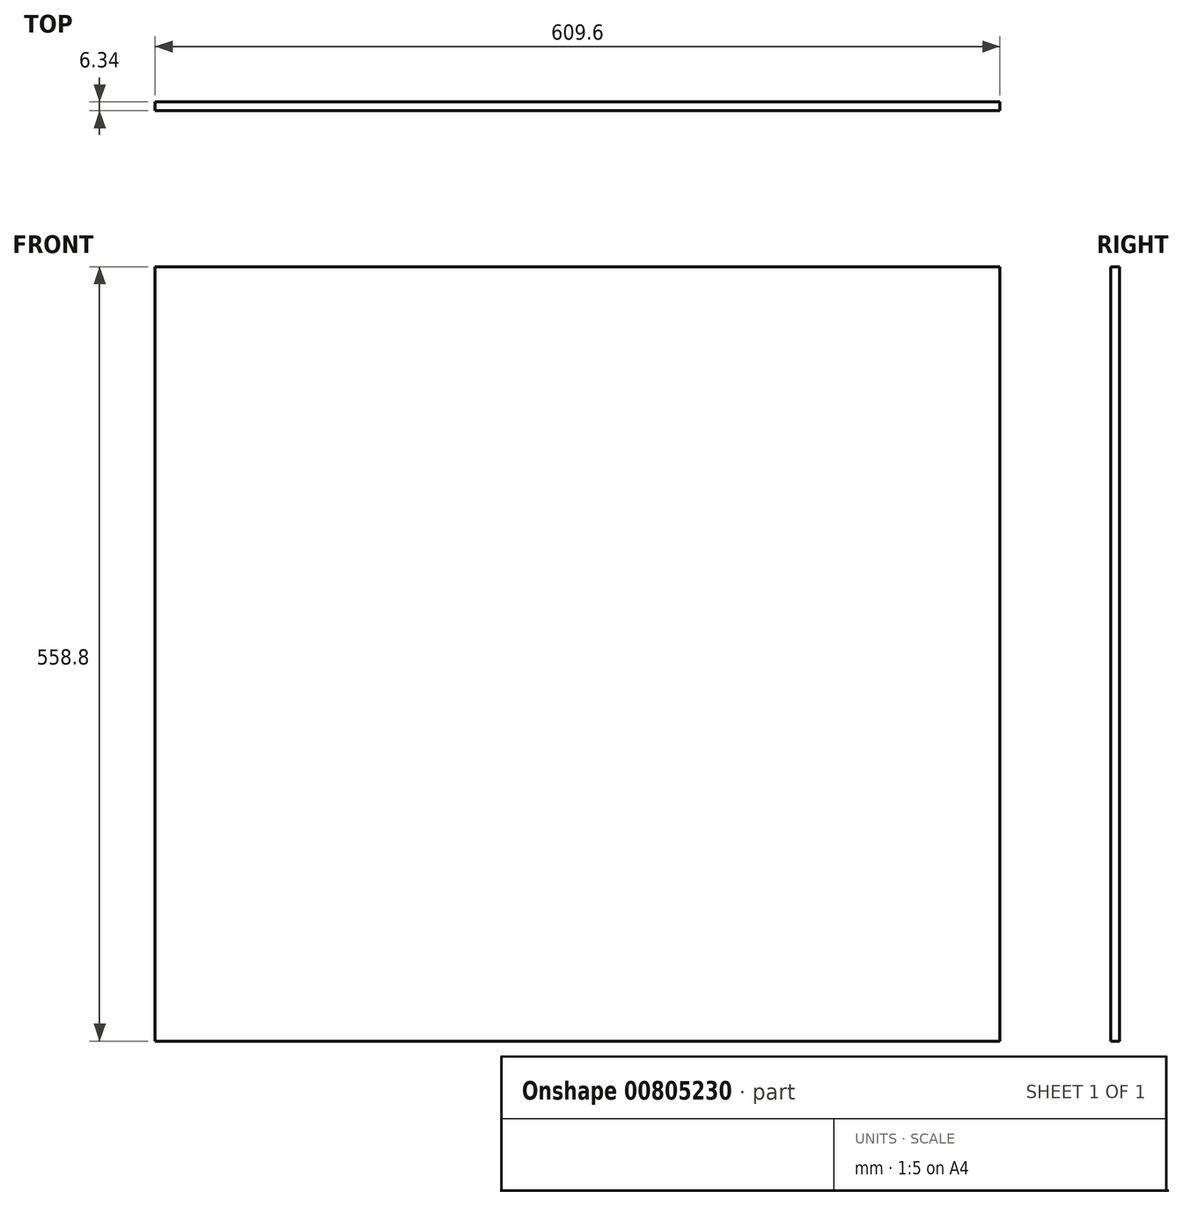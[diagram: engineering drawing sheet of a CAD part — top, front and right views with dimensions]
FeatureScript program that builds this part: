
annotation { "Feature Type Name" : "Feature", "Feature Type Description" : "" }
export const myFeature = defineFeature(function(context is Context, id is Id, definition is map)
    precondition{}
    {
        {
            var Q0;
            Q0=qCreatedBy(makeId("Front.planeOp"),FACE);
            var sketch = newSketch(context, id + "F0", { "sketchPlane" : qUnion([Q0])});
            skLineSegment(sketch, "E0.bottom", {"start": v(304.8, 279.4) * mm, "end": v(-304.8, 279.4) * mm});
            skLineSegment(sketch, "E0.top", {"start": v(304.8, -279.4) * mm, "end": v(-304.8, -279.4) * mm});
            skLineSegment(sketch, "E0.left", {"start": v(304.8, 279.4) * mm, "end": v(304.8, -279.4) * mm});
            skLineSegment(sketch, "E0.right", {"start": v(-304.8, 279.4) * mm, "end": v(-304.8, -279.4) * mm});
            skPoint(sketch, "E0.middle", {"position": v(0, 0) * mm});
            skSolve(sketch);
        }
        {
            var Q0;
            Q0=qSketchRegion(id+"F0",true);
            extrude(context, id + "F1", {"entities" : qUnion([Q0]), "endBound" : BoundingType.SYMMETRIC, "depth" : 6.35 * mm, "offsetDistance" : 25.4 * mm});
        }
    });
